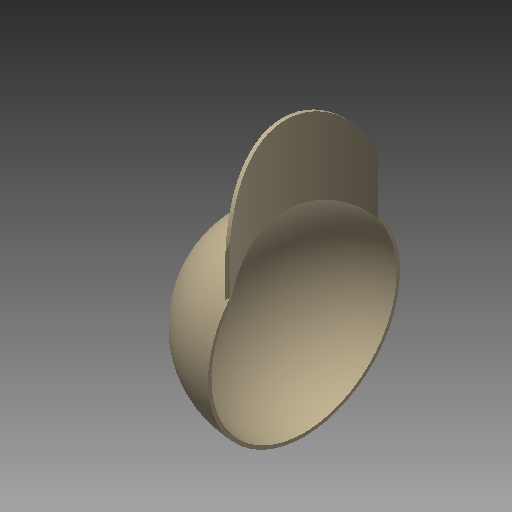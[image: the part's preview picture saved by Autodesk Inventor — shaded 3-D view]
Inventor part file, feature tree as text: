
AUTODESK INVENTOR PART (.ipt)
format: ipt  version: 2022 (Build 260153000, 153)  size: 232,448 bytes
history: native  units: mm (DEFAULTED — no unit token found)
features: sketch x4, plane x3, extrude x3, other x1, revolve x1, mirror x1, projected_geometry x1
ambient origin geometry x8: Origin, YZ Plane, XZ Plane, XY Plane, X Axis, Y Axis, Z Axis, Center Point
bodies: Solid1 (feature_tree)
feature tree (14):
  other  "iMan - 2D BODY"
  revolve  "Revolution1"  [1 undecoded]
  plane  "Work Plane1"
  plane  "Work Plane2"
  extrude  "Extrusion1"  TaperAngle=90.0deg  [1 undecoded]
  mirror  "Mirror1"
  extrude  "Extrusion2"  Depth=19.396283mm
  extrude  "Extrusion3"  Depth=3.556mm
  plane  "Work Plane3"
  sketch  "Sketch2"  dims[d1=10.0mm d25=96.981416mm]
  sketch  "Sketch4"  dims[d26=3.556mm d27=90.0deg]
  sketch  "Sketch5"  dims[d29=96.981416mm d30=19.396283mm]
  sketch  "Sketch6"  dims[d31=19.396283mm d32=3.556mm d33=25.4mm d34=0.0mm d35=25.4mm d36=0.0mm d37=25.4mm d38=0.0mm d39=-12.930856mm]
  projected_geometry  "Projected Loop1"
note: 2 required parameter values undecoded (feature->parameter linkage not recoverable at this tier; creation-order binding heuristic only, values carry confidence <= 0.55)